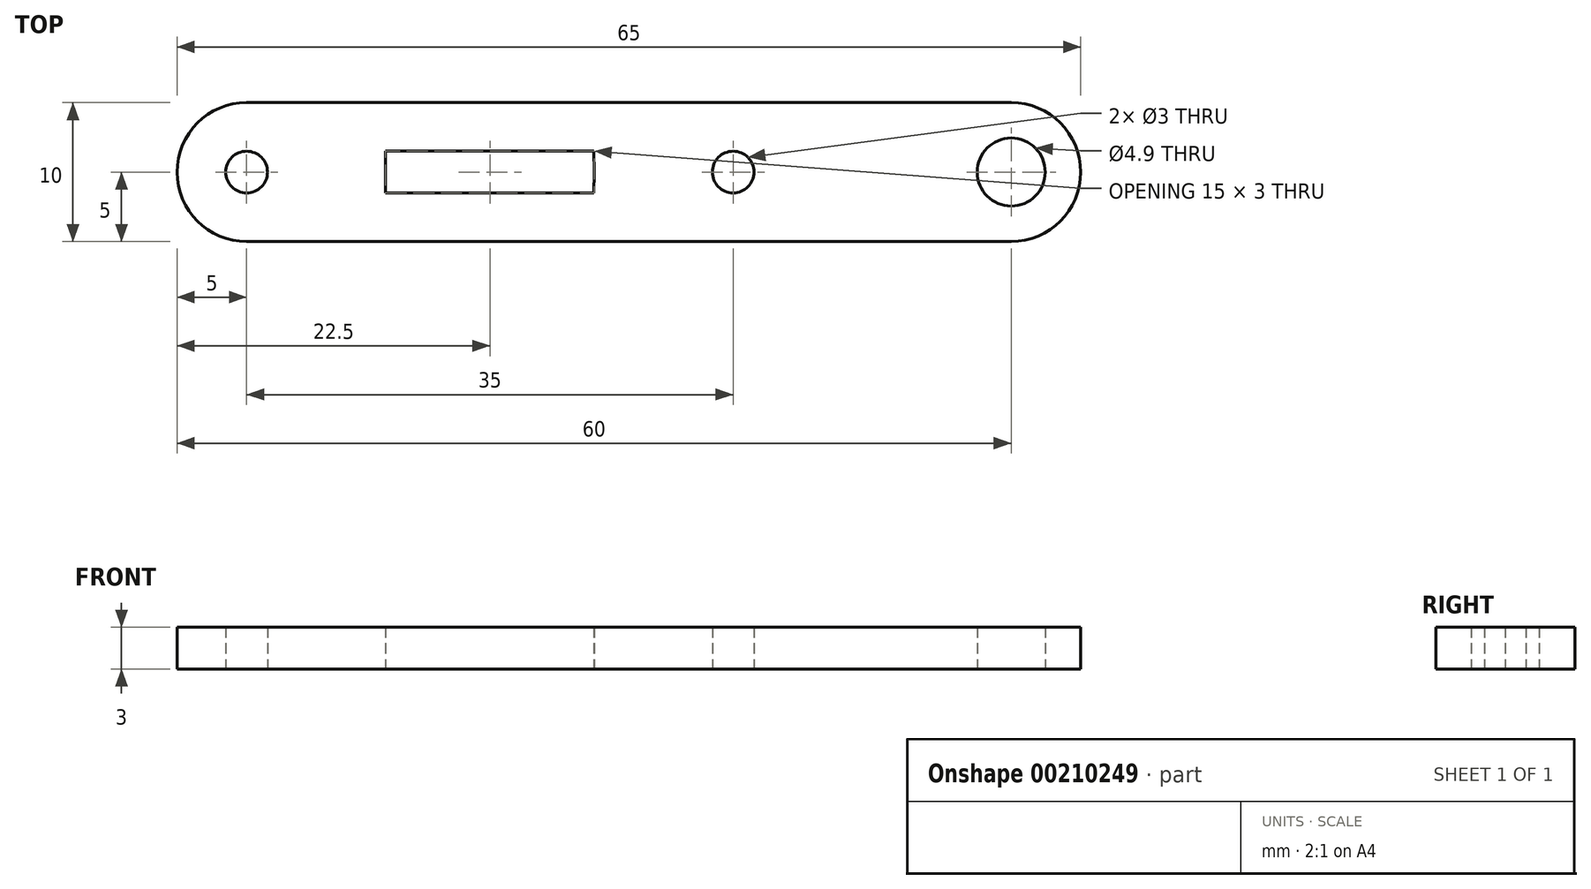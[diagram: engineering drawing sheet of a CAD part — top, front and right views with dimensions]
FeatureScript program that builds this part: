
annotation { "Feature Type Name" : "Feature", "Feature Type Description" : "" }
export const myFeature = defineFeature(function(context is Context, id is Id, definition is map)
    precondition{}
    {
        {
            var Q0;
            Q0=qCreatedBy(makeId("Top.planeOp"),FACE);
            var sketch = newSketch(context, id + "F0", { "sketchPlane" : qUnion([Q0])});
            skCircle(sketch, "E0", {"center": v(20, 0) * mm, "radius": 2.45 * mm});
            skArc(sketch, "E1", {"start": v(20, -5) * mm, "mid": v(25, 0) * mm, "end": v(20, 5) * mm});
            skLineSegment(sketch, "E2", {"start": v(20, 0) * mm, "end": v(17.55, 0) * mm});
            skLineSegment(sketch, "E3", {"start": v(-40, 0) * mm, "end": v(-40, 0) * mm});
            skLineSegment(sketch, "E4", {"start": v(-35, 5) * mm, "end": v(20, 5) * mm});
            skLineSegment(sketch, "E5.MirrorCS", {"start": v(-35, -5) * mm, "end": v(20, -5) * mm});
            skPoint(sketch, "E6", {"position": v(-10, 0) * mm});
            skPoint(sketch, "E7", {"position": v(-25, 0) * mm});
            skPoint(sketch, "E8", {"position": v(-35, 0) * mm});
            skCircle(sketch, "E9", {"center": v(0, 0) * mm, "radius": 1.5 * mm});
            skCircle(sketch, "E10", {"center": v(-35, 0) * mm, "radius": 1.5 * mm});
            skLineSegment(sketch, "E11", {"start": v(-25, 0) * mm, "end": v(-25, 1.5) * mm});
            skLineSegment(sketch, "E12", {"start": v(-25, 1.5) * mm, "end": v(-10.03, 1.5) * mm});
            skLineSegment(sketch, "E13", {"start": v(-10, 0) * mm, "end": v(-10.03, 1.5) * mm});
            skLineSegment(sketch, "E14.MirrorCS", {"start": v(-10, 0) * mm, "end": v(-10.03, -1.5) * mm});
            skLineSegment(sketch, "E15.MirrorCS", {"start": v(-25, -1.5) * mm, "end": v(-10.03, -1.5) * mm});
            skLineSegment(sketch, "E16.MirrorCS", {"start": v(-25, 0) * mm, "end": v(-25, -1.5) * mm});
            skPoint(sketch, "E17.visualSharp", {"position": v(-40, 5) * mm});
            skArc(sketch, "E17.filletArc", {"start": v(-35, 5) * mm, "mid": v(-38.54, 3.54) * mm, "end": v(-40, 0) * mm});
            skPoint(sketch, "E18.visualSharp", {"position": v(-40, -5) * mm});
            skArc(sketch, "E18.filletArc", {"start": v(-40, 0) * mm, "mid": v(-38.54, -3.54) * mm, "end": v(-35, -5) * mm});
            skSolve(sketch);
        }
        {
            var Q0;
            Q0=makeQuery(id+"F0.imprint","IMPRINT",FACE,{"disambiguationData":[TD([[makeQuery(id+"F0.imprint","IMPRINT",EDGE,{"derivedFrom":sQuery(id+"F0.wireOp",EDGE,"E0")}),-1.0]])]});
            extrude(context, id + "F1", {"entities" : qUnion([Q0]), "depth" : 3 * mm});
        }
    });
